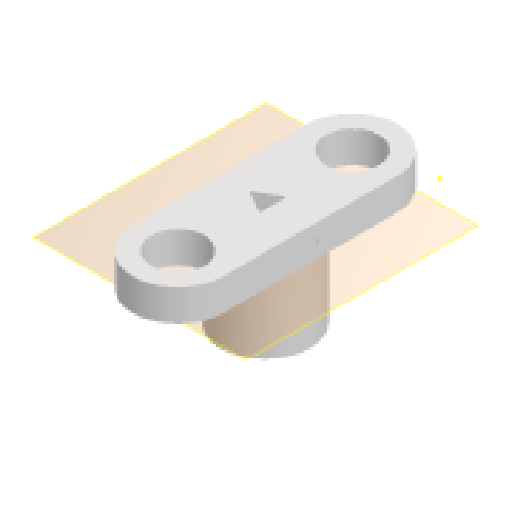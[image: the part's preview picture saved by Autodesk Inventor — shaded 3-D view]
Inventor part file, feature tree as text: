
AUTODESK INVENTOR PART (.ipt)
format: ipt  version: 2024.1 (Build 281209000, 209)  size: 157,184 bytes
history: native  units: mm
features: sketch x4, extrude x3, other x3, plane x1, reference x1, projected_geometry x1
ambient origin geometry x8: Origin, YZ Plane, XZ Plane, XY Plane, X Axis, Y Axis, Z Axis, Center Point
bodies: Volumenkörper1 (feature_tree)
feature tree (13):
  plane  "Arbeitsebene1"
  extrude  "Extrusion1"  Depth=10.0mm
  extrude  "Extrusion2"  Depth=17.0mm
  sketch  "Skizze3"  dims[d4=6.0mm d5=0.0mm d6=2.8mm]
  extrude  "Extrusion3"  Depth=2.8mm
  sketch  "Skizze1"  dims[d0=10.0mm d1=10.0mm]
  reference  "Referenz1"
  sketch  "Skizze2"  dims[d2=9.0mm d3=17.0mm]
  sketch  "Skizze4"  dims[d7=0.0mm d8=0.0mm d9=3.0mm d10=20.0mm d11=0.0mm]
  projected_geometry  "Projizierte Kontur1"
  other  "Application_Investigator_Lighsheet.iam"
  other  "40_XYZstage_micrometer_motorized_nema8_samplemount_lightsheet_screwed:1"
  other  "Baugruppe2"
